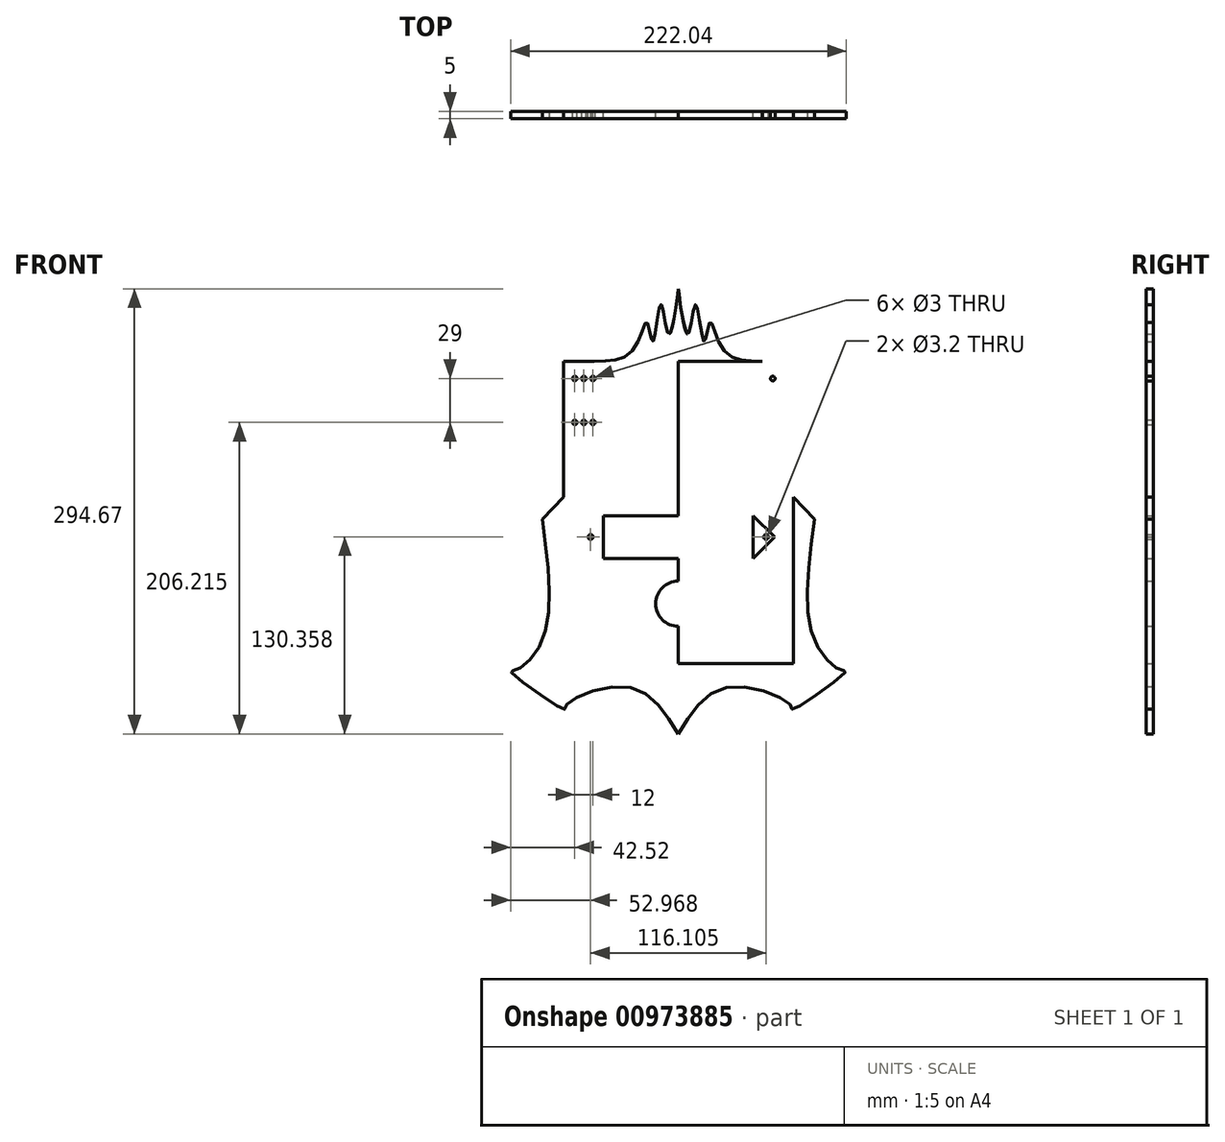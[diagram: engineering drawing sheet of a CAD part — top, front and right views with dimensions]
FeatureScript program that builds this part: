
annotation { "Feature Type Name" : "Feature", "Feature Type Description" : "" }
export const myFeature = defineFeature(function(context is Context, id is Id, definition is map)
    precondition{}
    {
        {
            var Q0;
            Q0=qCreatedBy(makeId("Front.planeOp"),FACE);
            var sketch = newSketch(context, id + "F0", { "sketchPlane" : qUnion([Q0])});
            skLineSegment(sketch, "E0", {"start": v(0, 136.24) * mm, "end": v(-76, 136.24) * mm});
            skLineSegment(sketch, "E1", {"start": v(-76, 136.24) * mm, "end": v(-76, -63.76) * mm});
            skLineSegment(sketch, "E2", {"start": v(-76, -63.76) * mm, "end": v(0, -63.76) * mm});
            skCircle(sketch, "E3", {"center": v(-68.5, 124.74) * mm, "radius": 1.5 * mm});
            skCircle(sketch, "E4.0.1.0", {"center": v(-68.5, 95.74) * mm, "radius": 1.5 * mm});
            skCircle(sketch, "E4.1.0.0", {"center": v(-62.5, 124.74) * mm, "radius": 1.5 * mm});
            skCircle(sketch, "E4.1.1.0", {"center": v(-62.5, 95.74) * mm, "radius": 1.5 * mm});
            skCircle(sketch, "E4.2.0.0", {"center": v(-56.5, 124.74) * mm, "radius": 1.5 * mm});
            skCircle(sketch, "E4.2.1.0", {"center": v(-56.5, 95.74) * mm, "radius": 1.5 * mm});
            skLineSegment(sketch, "E4.direction1", {"start": v(-68.5, 124.74) * mm, "end": v(-62.5, 124.74) * mm, "construction": true});
            skLineSegment(sketch, "E4.direction2", {"start": v(-68.5, 124.74) * mm, "end": v(-68.5, 95.74) * mm, "construction": true});
            skLineSegment(sketch, "E5", {"start": v(0, 5.74) * mm, "end": v(-49.5, 5.74) * mm});
            skLineSegment(sketch, "E6", {"start": v(-49.5, 5.74) * mm, "end": v(-49.5, 34.03) * mm});
            skLineSegment(sketch, "E7", {"start": v(-49.5, 34.03) * mm, "end": v(0, 34.03) * mm});
            skLineSegment(sketch, "E8", {"start": v(-49.5, 34.03) * mm, "end": v(-63.65, 19.89) * mm});
            skLineSegment(sketch, "E9", {"start": v(-63.65, 19.89) * mm, "end": v(-49.5, 5.74) * mm});
            skCircle(sketch, "E10", {"center": v(-58.05, 19.89) * mm, "radius": 1.6 * mm});
            skLineSegment(sketch, "E11", {"start": v(0, -39.25) * mm, "end": v(0, -9.26) * mm});
            skPoint(sketch, "E12.endSnap0", {"position": v(-76, 36.24) * mm});
            skLineSegment(sketch, "E13", {"start": v(-76, 46.24) * mm, "end": v(-90, 31.62) * mm});
            skFitSpline(sketch, "E14", {"points": [v(-90, 31.62) * mm, v(-90, -48.52) * mm, v(-108.78, -68.63) * mm, v(-110.96, -69.17) * mm, v(-75.64, -94.17) * mm, v(-74.55, -92) * mm, v(-33.8, -79.5) * mm, v(0, -110.47) * mm], "startDerivative": vector(50.8, -376.76) * mm, "endDerivative": vector(144.8, -236.93) * mm});
            skFitSpline(sketch, "E15", {"points": [v(-55.53, 136.24) * mm, v(-29.45, 144.38) * mm, v(-20.75, 161.78) * mm, v(-16.95, 149.26) * mm, v(-11.51, 173.73) * mm, v(-6.08, 154.16) * mm, v(0, 184.2) * mm, v(0, 184.2) * mm], "startDerivative": vector(169.48, 0.44) * mm, "endDerivative": vector(-2.4, 9) * mm});
            skPoint(sketch, "E16.orphan", {"position": v(0, 160.5) * mm});
            skPoint(sketch, "E17.orphan", {"position": v(0, -82.4) * mm});
            skLineSegment(sketch, "E18", {"start": v(0, 184.2) * mm, "end": v(0, -110.47) * mm});
            skFitSpline(sketch, "E19.MirrorCS", {"points": [v(55.53, 136.24) * mm, v(29.45, 144.38) * mm, v(20.75, 161.78) * mm, v(16.95, 149.26) * mm, v(11.51, 173.73) * mm, v(6.08, 154.16) * mm, v(0, 184.2) * mm, v(0, 184.2) * mm], "startDerivative": vector(-169.48, 0.44) * mm, "endDerivative": vector(2.4, 9) * mm});
            skLineSegment(sketch, "E20.MirrorCS", {"start": v(0, 136.24) * mm, "end": v(76, 136.24) * mm});
            skCircle(sketch, "E21.MirrorC", {"center": v(62.5, 124.74) * mm, "radius": 1.5 * mm});
            skCircle(sketch, "E22.MirrorC", {"center": v(56.5, 124.74) * mm, "radius": 1.5 * mm});
            skCircle(sketch, "E23.MirrorC", {"center": v(68.5, 124.74) * mm, "radius": 1.5 * mm});
            skCircle(sketch, "E24.MirrorC", {"center": v(68.5, 95.74) * mm, "radius": 1.5 * mm});
            skCircle(sketch, "E25.MirrorC", {"center": v(62.5, 95.74) * mm, "radius": 1.5 * mm});
            skCircle(sketch, "E26.MirrorC", {"center": v(56.5, 95.74) * mm, "radius": 1.5 * mm});
            skLineSegment(sketch, "E27.MirrorCS", {"start": v(76, 136.24) * mm, "end": v(76, -63.76) * mm});
            skLineSegment(sketch, "E28.MirrorCS", {"start": v(49.5, 34.03) * mm, "end": v(0, 34.03) * mm});
            skLineSegment(sketch, "E29.MirrorCS", {"start": v(49.5, 5.74) * mm, "end": v(49.5, 34.03) * mm});
            skLineSegment(sketch, "E30.MirrorCS", {"start": v(63.65, 19.89) * mm, "end": v(49.5, 5.74) * mm});
            skLineSegment(sketch, "E31.MirrorCS", {"start": v(49.5, 34.03) * mm, "end": v(63.65, 19.89) * mm});
            skLineSegment(sketch, "E32.MirrorCS", {"start": v(76, 46.24) * mm, "end": v(90, 31.62) * mm});
            skCircle(sketch, "E33.MirrorC", {"center": v(58.05, 19.89) * mm, "radius": 1.6 * mm});
            skFitSpline(sketch, "E34.MirrorCS", {"points": [v(90, 31.62) * mm, v(90, -48.52) * mm, v(108.78, -68.63) * mm, v(110.96, -69.17) * mm, v(75.64, -94.17) * mm, v(74.55, -92) * mm, v(33.8, -79.5) * mm, v(0, -110.47) * mm], "startDerivative": vector(-50.8, -376.76) * mm, "endDerivative": vector(-144.8, -236.93) * mm});
            skLineSegment(sketch, "E35.MirrorCS", {"start": v(76, -63.76) * mm, "end": v(0, -63.76) * mm});
            skPoint(sketch, "E36.orphan", {"position": v(0, -39.25) * mm});
            skCircle(sketch, "E37", {"center": v(0, -24.26) * mm, "radius": 15 * mm});
            skLineSegment(sketch, "E38", {"start": v(0, 5.74) * mm, "end": v(49.5, 5.74) * mm});
            skPoint(sketch, "E39.orphan", {"position": v(0, 34.03) * mm});
            skSolve(sketch);
        }
        {
            var Q0;
            {var subQ2=sQuery(id+"F0.wireOp",EDGE,"E2");Q0=makeQuery(id+"F0.imprint","IMPRINT",FACE,{"disambiguationData":[TD([[makeQuery(id+"F0.imprint","IMPRINT",EDGE,{"derivedFrom":subQ2}),-1.0]])]});}
            var Q1;
            {var subQ0=sQuery(id+"F0.wireOp",EDGE,"E2");Q1=makeQuery(id+"F0.imprint","IMPRINT",FACE,{"disambiguationData":[TD([[makeQuery(id+"F0.imprint","IMPRINT",EDGE,{"derivedFrom":subQ0}),1.0]])]});}
            var Q2;
            Q2=makeQuery(id+"F0.imprint","IMPRINT",FACE,{"disambiguationData":[TD([[makeQuery(id+"F0.imprint","IMPRINT",EDGE,{"derivedFrom":sQuery(id+"F0.wireOp",EDGE,"E21.MirrorC")}),1.0]])]});
            var Q3;
            {var subQ1=sQuery(id+"F0.wireOp",EDGE,"E32.MirrorCS");Q3=makeQuery(id+"F0.imprint","IMPRINT",FACE,{"disambiguationData":[TD([[makeQuery(id+"F0.imprint","IMPRINT",EDGE,{"derivedFrom":subQ1}),-1.0]])]});}
            var Q4;
            Q4=makeQuery(id+"F0.imprint","IMPRINT",FACE,{"disambiguationData":[TD([[makeQuery(id+"F0.imprint","IMPRINT",EDGE,{"derivedFrom":sQuery(id+"F0.wireOp",EDGE,"E29.MirrorCS")}),-1.0]])]});
            var Q5;
            Q5=makeQuery(id+"F0.imprint","IMPRINT",FACE,{"disambiguationData":[TD([[makeQuery(id+"F0.imprint","IMPRINT",EDGE,{"derivedFrom":sQuery(id+"F0.wireOp",EDGE,"E6")}),1.0]])]});
            var Q6;
            {var subQ3=sQuery(id+"F0.wireOp",EDGE,"E19.MirrorCS");Q6=makeQuery(id+"F0.imprint","IMPRINT",FACE,{"disambiguationData":[TD([[makeQuery(id+"F0.imprint","IMPRINT",EDGE,{"derivedFrom":subQ3}),1.0]])]});}
            var Q7;
            {var subQ3=sQuery(id+"F0.wireOp",EDGE,"E15");Q7=makeQuery(id+"F0.imprint","IMPRINT",FACE,{"disambiguationData":[TD([[makeQuery(id+"F0.imprint","IMPRINT",EDGE,{"derivedFrom":subQ3}),-1.0]])]});}
            extrude(context, id + "F1", {"entities" : qUnion([Q0, Q1, Q2, Q3, Q4, Q5, Q6, Q7]), "depth" : 5 * mm, "offsetDistance" : 25 * mm});
        }
    });
